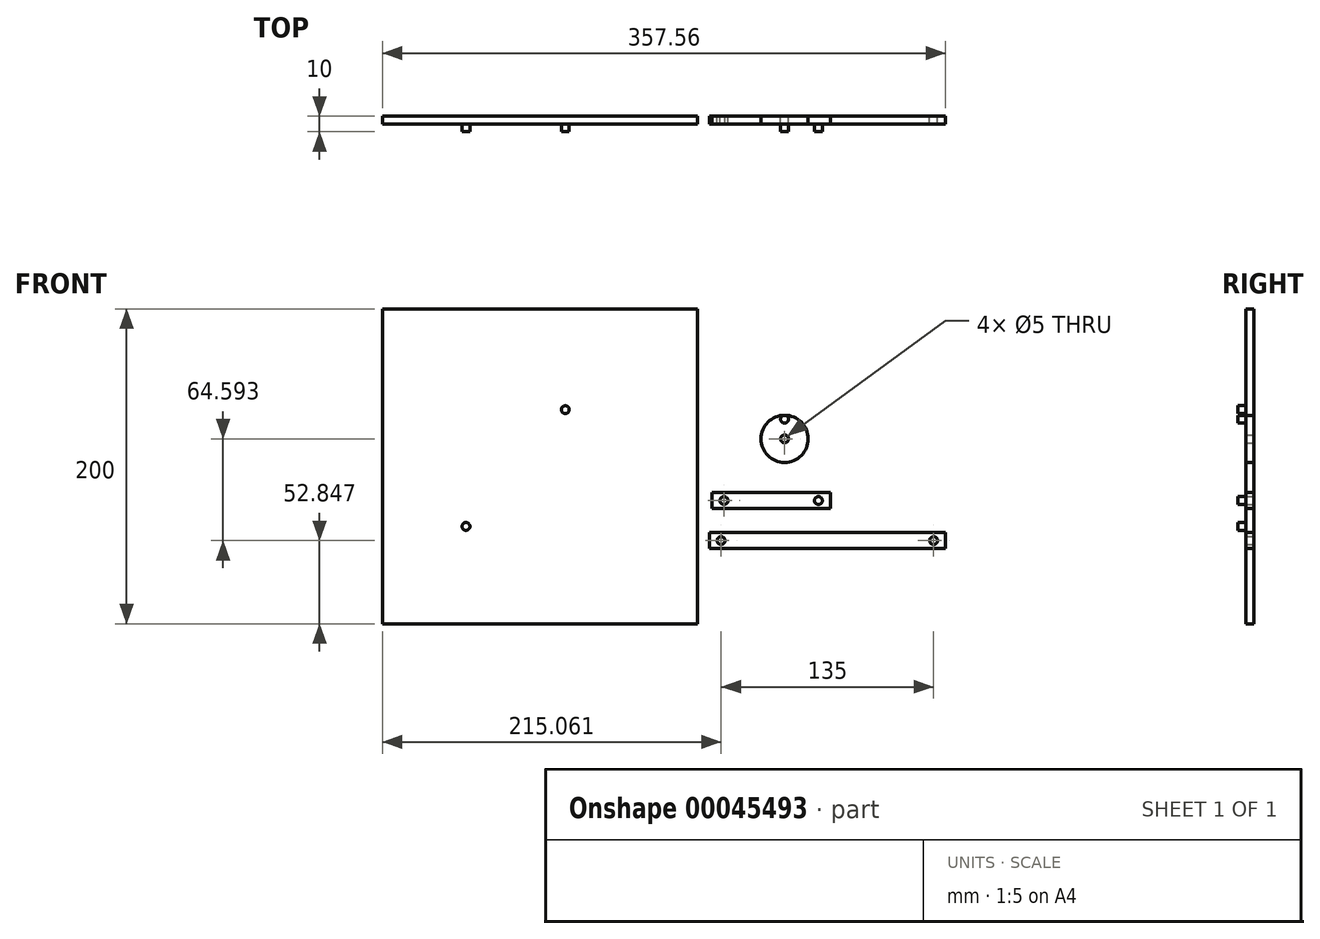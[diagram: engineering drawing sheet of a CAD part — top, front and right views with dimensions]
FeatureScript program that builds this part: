
annotation { "Feature Type Name" : "Feature", "Feature Type Description" : "" }
export const myFeature = defineFeature(function(context is Context, id is Id, definition is map)
    precondition{}
    {
        {
            var Q0;
            Q0=qCreatedBy(makeId("Front.planeOp"),FACE);
            var sketch = newSketch(context, id + "F0", { "sketchPlane" : qUnion([Q0])});
            skCircle(sketch, "E0", {"center": v(0, 0) * mm, "radius": 15 * mm});
            skCircle(sketch, "E1", {"center": v(0, 0) * mm, "radius": 2.5 * mm});
            skCircle(sketch, "E2", {"center": v(0, 12.5) * mm, "radius": 2.5 * mm});
            skLineSegment(sketch, "E3.bottom", {"start": v(-46, -34.18) * mm, "end": v(29, -34.18) * mm});
            skLineSegment(sketch, "E3.top", {"start": v(-46, -44.18) * mm, "end": v(29, -44.18) * mm});
            skLineSegment(sketch, "E3.left", {"start": v(-46, -34.18) * mm, "end": v(-46, -44.18) * mm});
            skLineSegment(sketch, "E3.right", {"start": v(29, -34.18) * mm, "end": v(29, -44.18) * mm});
            skCircle(sketch, "E4", {"center": v(-38.5, -39.18) * mm, "radius": 2.5 * mm});
            skCircle(sketch, "E5", {"center": v(21.5, -39.18) * mm, "radius": 2.5 * mm});
            skLineSegment(sketch, "E6.bottom", {"start": v(-47.85, -59.6) * mm, "end": v(102.15, -59.6) * mm});
            skLineSegment(sketch, "E6.top", {"start": v(-47.85, -69.6) * mm, "end": v(102.15, -69.6) * mm});
            skLineSegment(sketch, "E6.left", {"start": v(-47.85, -59.6) * mm, "end": v(-47.85, -69.6) * mm});
            skLineSegment(sketch, "E6.right", {"start": v(102.15, -59.6) * mm, "end": v(102.15, -69.6) * mm});
            skCircle(sketch, "E7", {"center": v(-40.35, -64.6) * mm, "radius": 2.5 * mm});
            skCircle(sketch, "E8", {"center": v(94.65, -64.6) * mm, "radius": 2.5 * mm});
            skSolve(sketch);
        }
        {
            var Q0;
            Q0=qCreatedBy(makeId("Front.planeOp"),FACE);
            var sketch = newSketch(context, id + "F1", { "sketchPlane" : qUnion([Q0])});
            skLineSegment(sketch, "E9.bottom", {"start": v(-255.4, 82.56) * mm, "end": v(-55.4, 82.56) * mm});
            skLineSegment(sketch, "E9.top", {"start": v(-255.4, -117.44) * mm, "end": v(-55.4, -117.44) * mm});
            skLineSegment(sketch, "E9.left", {"start": v(-255.4, 82.56) * mm, "end": v(-255.4, -117.44) * mm});
            skLineSegment(sketch, "E9.right", {"start": v(-55.4, 82.56) * mm, "end": v(-55.4, -117.44) * mm});
            skCircle(sketch, "E10", {"center": v(-202.37, -55.61) * mm, "radius": 2.5 * mm});
            skCircle(sketch, "E11", {"center": v(-139.27, 18.58) * mm, "radius": 2.5 * mm});
            skSolve(sketch);
        }
        {
            var Q0;
            Q0 = qSketchRegion(id + "F0", true);
            extrude(context, id + "F2", {"entities" : qUnion([Q0]), "depth" : 5 * mm});
        }
        {
            var Q0;
            Q0=makeQuery(id+"F1.imprint","IMPRINT",FACE,{"disambiguationData":[TD([[makeQuery(id+"F1.imprint","IMPRINT",EDGE,{"derivedFrom":sQuery(id+"F1.wireOp",EDGE,"E9.bottom")}),-1.0]])]});
            extrude(context, id + "F3", {"entities" : qUnion([Q0]), "depth" : 5 * mm});
        }
        {
            var Q0;
            Q0=makeQuery(id+"F1.imprint","IMPRINT",FACE,{"disambiguationData":[TD([[makeQuery(id+"F1.imprint","IMPRINT",EDGE,{"derivedFrom":sQuery(id+"F1.wireOp",EDGE,"E10")}),1.0]])]});
            extrude(context, id + "F4", {"entities" : qUnion([Q0]), "operationType" : NewBodyOperationType.ADD, "depth" : 10 * mm});
        }
        {
            var Q0;
            Q0=makeQuery(id+"F0.imprint","IMPRINT",FACE,{"disambiguationData":[TD([[makeQuery(id+"F0.imprint","IMPRINT",EDGE,{"derivedFrom":sQuery(id+"F0.wireOp",EDGE,"E2")}),1.0]])]});
            extrude(context, id + "F5", {"entities" : qUnion([Q0]), "operationType" : NewBodyOperationType.ADD, "depth" : 10 * mm});
        }
        {
            var Q0;
            Q0=makeQuery(id+"F0.imprint","IMPRINT",FACE,{"disambiguationData":[TD([[makeQuery(id+"F0.imprint","IMPRINT",EDGE,{"derivedFrom":sQuery(id+"F0.wireOp",EDGE,"E5")}),1.0]])]});
            extrude(context, id + "F6", {"entities" : qUnion([Q0]), "operationType" : NewBodyOperationType.ADD, "depth" : 10 * mm});
        }
        {
            var Q0;
            Q0=makeQuery(id+"F1.imprint","IMPRINT",FACE,{"disambiguationData":[TD([[makeQuery(id+"F1.imprint","IMPRINT",EDGE,{"derivedFrom":sQuery(id+"F1.wireOp",EDGE,"E11")}),1.0]])]});
            extrude(context, id + "F7", {"entities" : qUnion([Q0]), "operationType" : NewBodyOperationType.ADD, "depth" : 10 * mm});
        }
    });
